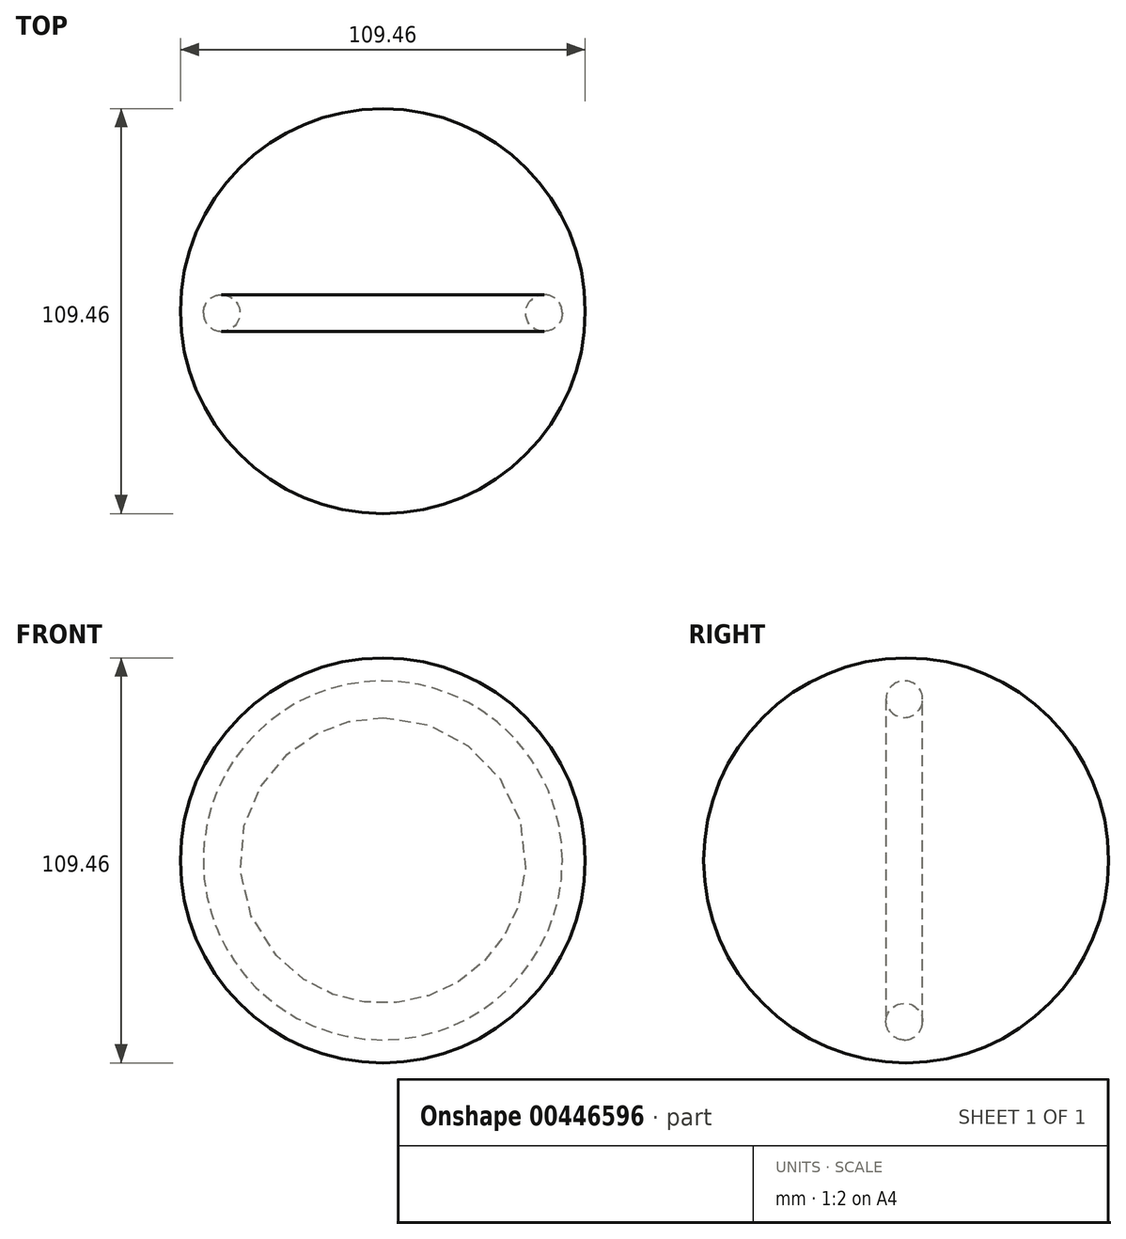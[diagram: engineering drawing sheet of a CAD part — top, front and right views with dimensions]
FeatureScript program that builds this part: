
annotation { "Feature Type Name" : "Feature", "Feature Type Description" : "" }
export const myFeature = defineFeature(function(context is Context, id is Id, definition is map)
    precondition{}
    {
        {
            var Q0;
            Q0=qCreatedBy(makeId("Top.planeOp"),FACE);
            var sketch = newSketch(context, id + "F0", { "sketchPlane" : qUnion([Q0])});
            skArc(sketch, "E0", {"start": v(0, 54.73) * mm, "mid": v(-54.73, 0) * mm, "end": v(0, -54.73) * mm});
            skArc(sketch, "E1", {"start": v(0, 32.66) * mm, "mid": v(-32.66, 0) * mm, "end": v(0, -32.66) * mm});
            skLineSegment(sketch, "E2", {"start": v(0, 54.73) * mm, "end": v(0, -54.73) * mm});
            skCircle(sketch, "E3", {"center": v(-43.57, -0.5) * mm, "radius": 4.95 * mm});
            skSolve(sketch);
        }
        {
            var Q0;
            {var subQ0=sQuery(id+"F0.wireOp",EDGE,"E1");Q0=makeQuery(id+"F0.imprint","IMPRINT",FACE,{"disambiguationData":[TD([[makeQuery(id+"F0.imprint","IMPRINT",EDGE,{"derivedFrom":subQ0}),1.0]])]});}
            var Q1;
            Q1 = qSketchRegion(id + "F0", true);
            var Q2;
            Q2=sQuery(id+"F0.wireOp",EDGE,"E2");
            revolve(context, id + "F1", {"entities" : qUnion([Q0, Q1]), "axis" : qUnion([Q2]), "revolveType" : RevolveType.FULL});
        }
        {
            var Q0;
            Q0=qCreatedBy(makeId("Top.planeOp"),FACE);
            var sketch = newSketch(context, id + "F2", { "sketchPlane" : qUnion([Q0])});
            skLineSegment(sketch, "E4.bottom", {"start": v(21.78, 23.3) * mm, "end": v(-21.78, 23.3) * mm});
            skLineSegment(sketch, "E4.top", {"start": v(21.78, -23.3) * mm, "end": v(-21.78, -23.3) * mm});
            skLineSegment(sketch, "E4.left", {"start": v(21.78, 23.3) * mm, "end": v(21.78, -23.3) * mm});
            skLineSegment(sketch, "E4.right", {"start": v(-21.78, 23.3) * mm, "end": v(-21.78, -23.3) * mm});
            skPoint(sketch, "E4.middle", {"position": v(0, 0) * mm});
            skSolve(sketch);
        }
        {
            var Q0;
            Q0=sQuery(id+"F2.wireOp",EDGE,"E4.left");
            var Q1;
            Q1=sQuery(id+"F2.wireOp",EDGE,"E4.top");
            var Q2;
            Q2=sQuery(id+"F2.wireOp",EDGE,"E4.right");
            var Q3;
            Q3=sQuery(id+"F2.wireOp",EDGE,"E4.bottom");
            extrude(context, id + "F3", {"bodyType" : ToolBodyType.SURFACE, "surfaceEntities" : qUnion([Q0, Q1, Q2, Q3]), "endBound" : BoundingType.THROUGH_ALL, "depth" : 25.4 * mm, "hasSecondDirection" : true, "secondDirectionBound" : SecondDirectionBoundingType.THROUGH_ALL, "secondDirectionOppositeDirection" : true, "secondDirectionDepth" : 25.4 * mm});
        }
    });
